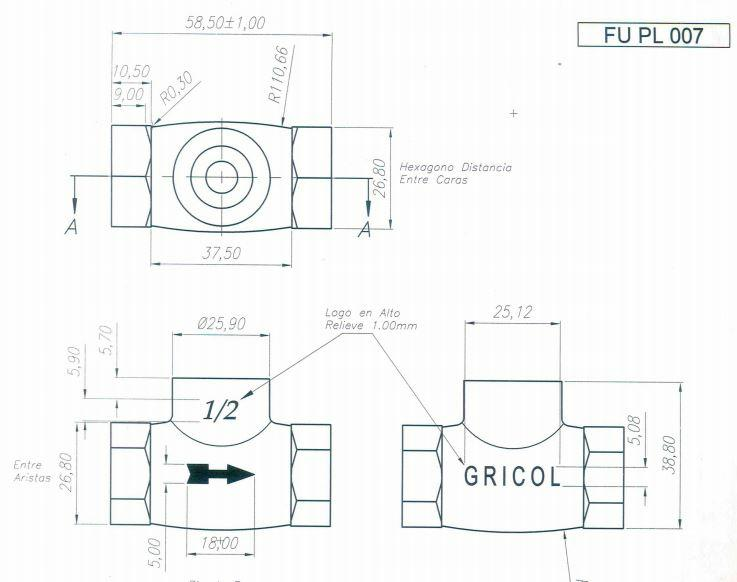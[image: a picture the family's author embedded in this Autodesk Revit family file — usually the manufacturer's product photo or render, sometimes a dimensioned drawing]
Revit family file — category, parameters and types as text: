
# Revit family: 01-1134-00 REGISTRO DUCHA CON REGADERA KRISTHAL
name_source: partatom
category: Plumbing Fixtures
revit_build: Autodesk Revit 2018 (Build: 20170223_1515(x64)
units: mm (PartAtom-declared; Revit-internal decimal feet)

## family parameters
Cut with Voids When Loaded = No
Host = Face
OmniClass Number = 23.31.11.00
Part Type = Normal
Room Calculation Point = No
Round Connector Dimension = Use Diameter
Shared = No

## types (1)
- 01-1134-00
    Alto Manija = 66 mm
    Alto manija = 66 mm
    Ancho ducha = 150 mm
    Ancho manija = 60 mm  [stored 0.19685 ft]
    CW Connection = Yes
    Default Elevation = 0 mm  [stored 0 ft]
    Description = Mezclador ducha
    Escudo = 71 mm
    HW Connection = Yes
    Laton = Laton
    Link Ficha Tecnica = No encontrada en internet
    Manufacturer = Gricol
    Metal Laton Cromado = Metal Laton Cromado
    Model = 01-1134-00
    Plastico - ABS Cromado = Plastico - ABS Cromado
    Plastico acrilico transparente = Plastico Acrilico Transparente
    Product Name = REGISTRO DUCHA CON REGADERA KRISTHAL
    Type Image = LOGO-01.jpg
    URL = https://www.gricol.com
    Vent Connection = No
    Waste Connection = No

note: [stored X ft] marks values corroborated as IEEE doubles in the binary element streams (Revit-internal decimal feet)

## geometry (parser evidence)
native form markers: Blend x4, Sweep x23
no freeform markers — native parametric forms only
